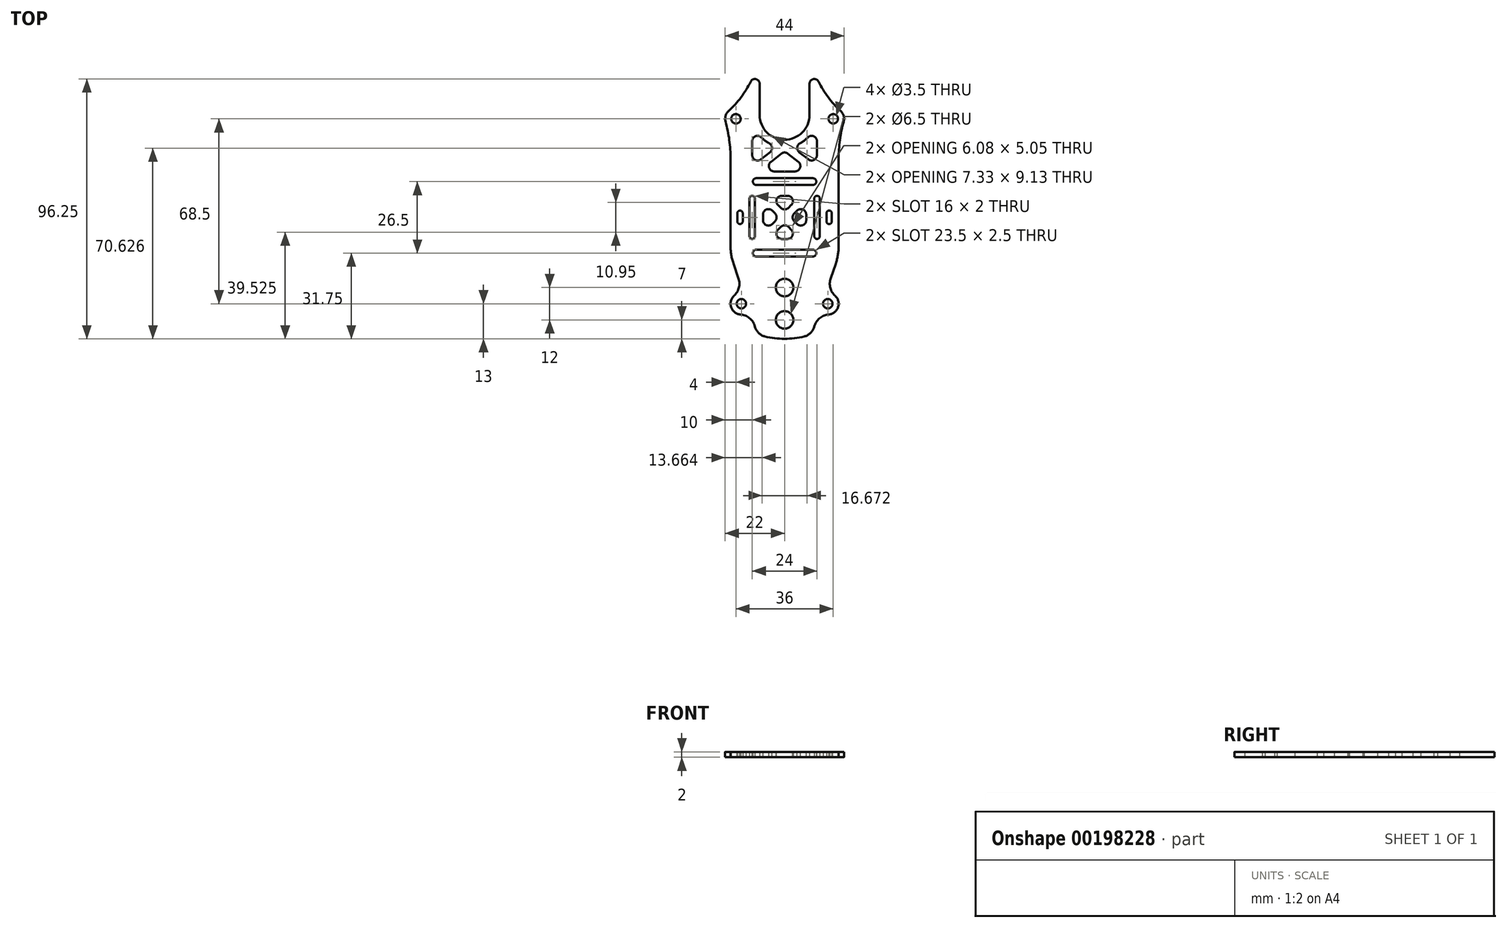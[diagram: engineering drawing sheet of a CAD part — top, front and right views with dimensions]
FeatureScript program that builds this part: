
annotation { "Feature Type Name" : "Feature", "Feature Type Description" : "" }
export const myFeature = defineFeature(function(context is Context, id is Id, definition is map)
    precondition{}
    {
        {
            var Q0;
            Q0=qCreatedBy(makeId("Top.planeOp"),FACE);
            var sketch = newSketch(context, id + "F0", { "sketchPlane" : qUnion([Q0])});
            skArc(sketch, "E0", {"start": v(-20.7, 39.46) * mm, "mid": v(-21.84, 37.62) * mm, "end": v(-21.86, 35.44) * mm});
            skLineSegment(sketch, "E1", {"start": v(-18.93, -17.14) * mm, "end": v(-17.05, -22.66) * mm});
            skLineSegment(sketch, "E2", {"start": v(0, 24) * mm, "end": v(0, -60) * mm, "construction": true});
            skCircle(sketch, "E3", {"center": v(-16, -32) * mm, "radius": 1.75 * mm});
            skArc(sketch, "E4.MirrorCS", {"start": v(20.7, 39.46) * mm, "mid": v(21.84, 37.62) * mm, "end": v(21.86, 35.44) * mm});
            skCircle(sketch, "E5.MirrorC", {"center": v(16, -32) * mm, "radius": 1.75 * mm});
            skLineSegment(sketch, "E6.MirrorCS", {"start": v(18.93, -17.14) * mm, "end": v(17.05, -22.66) * mm});
            skCircle(sketch, "E7", {"center": v(-18, 36.5) * mm, "radius": 1.75 * mm});
            skCircle(sketch, "E8.MirrorC", {"center": v(18, 36.5) * mm, "radius": 1.75 * mm});
            skCircle(sketch, "E9", {"center": v(0, -38) * mm, "radius": 3.25 * mm});
            skArc(sketch, "E10", {"start": v(-7.28, -44.13) * mm, "mid": v(-3.66, -44.78) * mm, "end": v(0, -45) * mm});
            skLineSegment(sketch, "E11.trimOffspring", {"start": v(-20, 21.67) * mm, "end": v(-20, -10.69) * mm});
            skArc(sketch, "E12", {"start": v(16.32, -35.99) * mm, "mid": v(19.79, -33.3) * mm, "end": v(18.7, -29.04) * mm});
            skArc(sketch, "E13.filletArc", {"start": v(16.32, -35.99) * mm, "mid": v(13.12, -37.23) * mm, "end": v(11.13, -40.03) * mm});
            skArc(sketch, "E14.filletArc", {"start": v(17.05, -22.66) * mm, "mid": v(16.92, -26.1) * mm, "end": v(18.7, -29.04) * mm});
            skArc(sketch, "E15.MirrorCS", {"start": v(-16.32, -35.99) * mm, "mid": v(-13.12, -37.23) * mm, "end": v(-11.13, -40.03) * mm});
            skArc(sketch, "E16.MirrorCS", {"start": v(-16.32, -35.99) * mm, "mid": v(-19.79, -33.3) * mm, "end": v(-18.7, -29.04) * mm});
            skArc(sketch, "E17.MirrorCS", {"start": v(-17.05, -22.66) * mm, "mid": v(-16.92, -26.1) * mm, "end": v(-18.7, -29.04) * mm});
            skLineSegment(sketch, "E18", {"start": v(-11.13, -40.03) * mm, "end": v(-10.84, -40.89) * mm});
            skLineSegment(sketch, "E19", {"start": v(11.13, -40.03) * mm, "end": v(10.84, -40.89) * mm});
            skLineSegment(sketch, "E20", {"start": v(-17.05, -22.66) * mm, "end": v(-11.13, -40.03) * mm, "construction": true});
            skLineSegment(sketch, "E21", {"start": v(17.05, -22.66) * mm, "end": v(11.13, -40.03) * mm, "construction": true});
            skArc(sketch, "E22", {"start": v(-9.25, 49.5) * mm, "mid": v(-10.6, 51.2) * mm, "end": v(-12.57, 50.27) * mm});
            skArc(sketch, "E23", {"start": v(-20.7, 39.46) * mm, "mid": v(-16.12, 44.48) * mm, "end": v(-12.57, 50.27) * mm});
            skArc(sketch, "E24.MirrorCS", {"start": v(9.25, 49.5) * mm, "mid": v(10.6, 51.2) * mm, "end": v(12.57, 50.27) * mm});
            skArc(sketch, "E25.MirrorCS", {"start": v(20.7, 39.46) * mm, "mid": v(16.12, 44.48) * mm, "end": v(12.57, 50.27) * mm});
            skPoint(sketch, "E26.visualSharp", {"position": v(-10, -43.34) * mm});
            skArc(sketch, "E26.filletArc", {"start": v(-10.84, -40.89) * mm, "mid": v(-9.47, -42.97) * mm, "end": v(-7.28, -44.13) * mm});
            skPoint(sketch, "E27.visualSharp", {"position": v(10, -43.34) * mm});
            skArc(sketch, "E27.filletArc", {"start": v(7.28, -44.13) * mm, "mid": v(9.47, -42.97) * mm, "end": v(10.84, -40.89) * mm});
            skLineSegment(sketch, "E28", {"start": v(-16.5, 1.5) * mm, "end": v(-16.5, -1.5) * mm, "construction": true});
            skArc(sketch, "E29.0.startCap", {"start": v(-17.5, 1.5) * mm, "mid": v(-16.5, 2.5) * mm, "end": v(-15.5, 1.5) * mm});
            skArc(sketch, "E29.0.endCap", {"start": v(-15.5, -1.5) * mm, "mid": v(-16.5, -2.5) * mm, "end": v(-17.5, -1.5) * mm});
            skLineSegment(sketch, "E29.0.left", {"start": v(-15.5, 1.5) * mm, "end": v(-15.5, -1.5) * mm});
            skLineSegment(sketch, "E29.0.right", {"start": v(-17.5, 1.5) * mm, "end": v(-17.5, -1.5) * mm});
            skLineSegment(sketch, "E30.MirrorCS", {"start": v(16.5, 1.5) * mm, "end": v(16.5, -1.5) * mm, "construction": true});
            skLineSegment(sketch, "E31.MirrorCS", {"start": v(15.5, 1.5) * mm, "end": v(15.5, -1.5) * mm});
            skLineSegment(sketch, "E32.MirrorCS", {"start": v(17.5, 1.5) * mm, "end": v(17.5, -1.5) * mm});
            skArc(sketch, "E33.MirrorCS", {"start": v(17.5, 1.5) * mm, "mid": v(16.5, 2.5) * mm, "end": v(15.5, 1.5) * mm});
            skArc(sketch, "E34.MirrorCS", {"start": v(15.5, -1.5) * mm, "mid": v(16.5, -2.5) * mm, "end": v(17.5, -1.5) * mm});
            skArc(sketch, "E35", {"start": v(-20, 21.67) * mm, "mid": v(-20.47, 28.62) * mm, "end": v(-21.86, 35.44) * mm});
            skArc(sketch, "E36.MirrorCS", {"start": v(20, 21.67) * mm, "mid": v(20.47, 28.62) * mm, "end": v(21.86, 35.44) * mm});
            skCircle(sketch, "E37", {"center": v(0, -38) * mm, "radius": 4.5 * mm, "construction": true});
            skLineSegment(sketch, "E38", {"start": v(20, 21.67) * mm, "end": v(20, -10.69) * mm});
            skLineSegment(sketch, "E39", {"start": v(-10.5, 13.25) * mm, "end": v(10.5, 13.25) * mm, "construction": true});
            skLineSegment(sketch, "E40", {"start": v(-10.5, -13.25) * mm, "end": v(10.5, -13.25) * mm, "construction": true});
            skArc(sketch, "E41.0.startCap", {"start": v(-10.5, 12) * mm, "mid": v(-11.75, 13.25) * mm, "end": v(-10.5, 14.5) * mm});
            skArc(sketch, "E41.0.endCap", {"start": v(10.5, 14.5) * mm, "mid": v(11.75, 13.25) * mm, "end": v(10.5, 12) * mm});
            skLineSegment(sketch, "E41.0.left", {"start": v(-10.5, 14.5) * mm, "end": v(10.5, 14.5) * mm});
            skLineSegment(sketch, "E41.0.right", {"start": v(-10.5, 12) * mm, "end": v(10.5, 12) * mm});
            skArc(sketch, "E41.1.startCap", {"start": v(-10.5, -14.5) * mm, "mid": v(-11.75, -13.25) * mm, "end": v(-10.5, -12) * mm});
            skArc(sketch, "E41.1.endCap", {"start": v(10.5, -12) * mm, "mid": v(11.75, -13.25) * mm, "end": v(10.5, -14.5) * mm});
            skLineSegment(sketch, "E41.1.left", {"start": v(-10.5, -12) * mm, "end": v(10.5, -12) * mm});
            skLineSegment(sketch, "E41.1.right", {"start": v(-10.5, -14.5) * mm, "end": v(10.5, -14.5) * mm});
            skPoint(sketch, "E42.visualSharp", {"position": v(-20, -14) * mm});
            skArc(sketch, "E42.filletArc", {"start": v(-20, -10.69) * mm, "mid": v(-19.73, -13.96) * mm, "end": v(-18.93, -17.14) * mm});
            skPoint(sketch, "E43.visualSharp", {"position": v(20, -14) * mm});
            skArc(sketch, "E43.filletArc", {"start": v(18.93, -17.14) * mm, "mid": v(19.73, -13.96) * mm, "end": v(20, -10.69) * mm});
            skLineSegment(sketch, "E44", {"start": v(-12, 7) * mm, "end": v(-12, -7) * mm, "construction": true});
            skLineSegment(sketch, "E45.MirrorCS", {"start": v(12, 7) * mm, "end": v(12, -7) * mm, "construction": true});
            skArc(sketch, "E46.0.startCap", {"start": v(-13, 7) * mm, "mid": v(-12, 8) * mm, "end": v(-11, 7) * mm});
            skArc(sketch, "E46.0.endCap", {"start": v(-11, -7) * mm, "mid": v(-12, -8) * mm, "end": v(-13, -7) * mm});
            skLineSegment(sketch, "E46.0.left", {"start": v(-11, 7) * mm, "end": v(-11, -7) * mm});
            skLineSegment(sketch, "E46.0.right", {"start": v(-13, 7) * mm, "end": v(-13, -7) * mm});
            skArc(sketch, "E46.3.startCap", {"start": v(11, 7) * mm, "mid": v(12, 8) * mm, "end": v(13, 7) * mm});
            skArc(sketch, "E46.3.endCap", {"start": v(13, -7) * mm, "mid": v(12, -8) * mm, "end": v(11, -7) * mm});
            skLineSegment(sketch, "E46.3.left", {"start": v(13, 7) * mm, "end": v(13, -7) * mm});
            skLineSegment(sketch, "E46.3.right", {"start": v(11, 7) * mm, "end": v(11, -7) * mm});
            skPoint(sketch, "E47.startSnap0", {"position": v(-16.5, 2.5) * mm});
            skArc(sketch, "E48.trimOffspring", {"start": v(0, -45) * mm, "mid": v(3.66, -44.78) * mm, "end": v(7.28, -44.13) * mm});
            skCircle(sketch, "E49", {"center": v(0, -26) * mm, "radius": 3.25 * mm});
            skLineSegment(sketch, "E50", {"start": v(-9.25, 49.5) * mm, "end": v(-9.25, 38) * mm});
            skLineSegment(sketch, "E51.MirrorCS", {"start": v(9.25, 49.5) * mm, "end": v(9.25, 38) * mm});
            skArc(sketch, "E52", {"start": v(-9.25, 38) * mm, "mid": v(0, 28.75) * mm, "end": v(9.25, 38) * mm});
            skSolve(sketch);
        }
        {
            var Q0;
            Q0=qSketchRegion(id+"F0",true);
            var Q1;
            Q1=makeQuery(id+"F0.imprint","IMPRINT",FACE,{"disambiguationData":[TD([[makeQuery(id+"F0.imprint","IMPRINT",EDGE,{"derivedFrom":sQuery(id+"F0.wireOp",EDGE,"f439a884-37bc-483a-9020-57d0572b4fa8.sketch_text.stroke-0")}),-1.0]])]});
            var Q2;
            Q2=makeQuery(id+"F0.imprint","IMPRINT",FACE,{"disambiguationData":[TD([[makeQuery(id+"F0.imprint","IMPRINT",EDGE,{"derivedFrom":sQuery(id+"F0.wireOp",EDGE,"f439a884-37bc-483a-9020-57d0572b4fa8.sketch_text.stroke-27")}),-1.0]])]});
            extrude(context, id + "F1", {"entities" : qUnion([Q0, Q1, Q2]), "depth" : 2 * mm});
        }
        {
            var Q0;
            Q0=makeQuery(id+"F1.opExtrude","CAP_FACE",FACE,{"disambiguationData":[OSD([sQuery(id+"F0.wireOp",EDGE,"E0"),sQuery(id+"F0.wireOp",EDGE,"E1"),sQuery(id+"F0.wireOp",EDGE,"E3"),sQuery(id+"F0.wireOp",EDGE,"E4.MirrorCS"),sQuery(id+"F0.wireOp",EDGE,"E5.MirrorC"),sQuery(id+"F0.wireOp",EDGE,"E6.MirrorCS"),sQuery(id+"F0.wireOp",EDGE,"E7"),sQuery(id+"F0.wireOp",EDGE,"E8.MirrorC"),sQuery(id+"F0.wireOp",EDGE,"E9"),sQuery(id+"F0.wireOp",EDGE,"E10"),sQuery(id+"F0.wireOp",EDGE,"E11.trimOffspring"),sQuery(id+"F0.wireOp",EDGE,"E12"),sQuery(id+"F0.wireOp",EDGE,"E13.filletArc"),sQuery(id+"F0.wireOp",EDGE,"E14.filletArc"),sQuery(id+"F0.wireOp",EDGE,"E15.MirrorCS"),sQuery(id+"F0.wireOp",EDGE,"E16.MirrorCS"),sQuery(id+"F0.wireOp",EDGE,"E17.MirrorCS"),sQuery(id+"F0.wireOp",EDGE,"E18"),sQuery(id+"F0.wireOp",EDGE,"E19"),sQuery(id+"F0.wireOp",EDGE,"E22"),sQuery(id+"F0.wireOp",EDGE,"E23"),sQuery(id+"F0.wireOp",EDGE,"E24.MirrorCS"),sQuery(id+"F0.wireOp",EDGE,"E25.MirrorCS"),sQuery(id+"F0.wireOp",EDGE,"E26.filletArc"),sQuery(id+"F0.wireOp",EDGE,"E27.filletArc"),sQuery(id+"F0.wireOp",EDGE,"E29.0.startCap"),sQuery(id+"F0.wireOp",EDGE,"E29.0.endCap"),sQuery(id+"F0.wireOp",EDGE,"E29.0.left"),sQuery(id+"F0.wireOp",EDGE,"E29.0.right"),sQuery(id+"F0.wireOp",EDGE,"E31.MirrorCS"),sQuery(id+"F0.wireOp",EDGE,"E32.MirrorCS"),sQuery(id+"F0.wireOp",EDGE,"E33.MirrorCS"),sQuery(id+"F0.wireOp",EDGE,"E34.MirrorCS"),sQuery(id+"F0.wireOp",EDGE,"E35"),sQuery(id+"F0.wireOp",EDGE,"E36.MirrorCS"),sQuery(id+"F0.wireOp",EDGE,"E38"),sQuery(id+"F0.wireOp",EDGE,"E41.0.startCap"),sQuery(id+"F0.wireOp",EDGE,"E41.0.endCap"),sQuery(id+"F0.wireOp",EDGE,"E41.0.left"),sQuery(id+"F0.wireOp",EDGE,"E41.0.right"),sQuery(id+"F0.wireOp",EDGE,"E41.1.startCap"),sQuery(id+"F0.wireOp",EDGE,"E41.1.endCap"),sQuery(id+"F0.wireOp",EDGE,"E41.1.left"),sQuery(id+"F0.wireOp",EDGE,"E41.1.right"),sQuery(id+"F0.wireOp",EDGE,"E42.filletArc"),sQuery(id+"F0.wireOp",EDGE,"E43.filletArc"),sQuery(id+"F0.wireOp",EDGE,"E46.0.startCap"),sQuery(id+"F0.wireOp",EDGE,"E46.0.endCap"),sQuery(id+"F0.wireOp",EDGE,"E46.0.left"),sQuery(id+"F0.wireOp",EDGE,"E46.0.right"),sQuery(id+"F0.wireOp",EDGE,"E46.3.startCap"),sQuery(id+"F0.wireOp",EDGE,"E46.3.endCap"),sQuery(id+"F0.wireOp",EDGE,"E46.3.left"),sQuery(id+"F0.wireOp",EDGE,"E46.3.right"),sQuery(id+"F0.wireOp",EDGE,"E48.trimOffspring"),sQuery(id+"F0.wireOp",EDGE,"E49"),sQuery(id+"F0.wireOp",EDGE,"E50"),sQuery(id+"F0.wireOp",EDGE,"E51.MirrorCS"),sQuery(id+"F0.wireOp",EDGE,"E52")])],"isStart":false});
            var sketch = newSketch(context, id + "F2", { "sketchPlane" : qUnion([Q0])});
            skLineSegment(sketch, "E53.bottom", {"start": v(-1.05, 8) * mm, "end": v(1.05, 8) * mm});
            skLineSegment(sketch, "E53.top", {"start": v(-1.05, -8) * mm, "end": v(1.05, -8) * mm});
            skLineSegment(sketch, "E53.left", {"start": v(-8, 1.05) * mm, "end": v(-8, -1.05) * mm});
            skLineSegment(sketch, "E53.right", {"start": v(8, 1.05) * mm, "end": v(8, -1.05) * mm});
            skLineSegment(sketch, "E54.bottom", {"start": v(-12, 36) * mm, "end": v(12, 36) * mm, "construction": true});
            skLineSegment(sketch, "E54.top", {"start": v(-3.83, 17) * mm, "end": v(3.83, 17) * mm});
            skLineSegment(sketch, "E54.left", {"start": v(-12, 28.2) * mm, "end": v(-12, 23.05) * mm});
            skLineSegment(sketch, "E54.right", {"start": v(12, 28.2) * mm, "end": v(12, 23.05) * mm});
            skArc(sketch, "E55", {"start": v(-8.57, 29.6) * mm, "mid": v(-7.22, 28.42) * mm, "end": v(-5.71, 27.45) * mm});
            skPoint(sketch, "E55.centerSnap0", {"position": v(0, 36) * mm});
            skLineSegment(sketch, "E56", {"start": v(-8, 8) * mm, "end": v(8, -8) * mm, "construction": true});
            skLineSegment(sketch, "E57", {"start": v(-8, -8) * mm, "end": v(8, 8) * mm, "construction": true});
            skLineSegment(sketch, "E58", {"start": v(-12, 36) * mm, "end": v(12, 17) * mm, "construction": true});
            skLineSegment(sketch, "E59", {"start": v(-12, 17) * mm, "end": v(12, 36) * mm, "construction": true});
            skLineSegment(sketch, "E60", {"start": v(1.24, 23.6) * mm, "end": v(5.08, 20.57) * mm});
            skLineSegment(sketch, "E61", {"start": v(5.42, 24.12) * mm, "end": v(8.76, 21.48) * mm});
            skLineSegment(sketch, "E62.MirrorCS", {"start": v(-5.42, 24.12) * mm, "end": v(-8.76, 21.48) * mm});
            skLineSegment(sketch, "E63.MirrorCS", {"start": v(-1.24, 23.6) * mm, "end": v(-5.08, 20.57) * mm});
            skArc(sketch, "E64.trimOffspring", {"start": v(5.71, 27.45) * mm, "mid": v(7.22, 28.42) * mm, "end": v(8.57, 29.6) * mm});
            skPoint(sketch, "E65.orphan", {"position": v(2, 26.17) * mm});
            skPoint(sketch, "E66.orphan", {"position": v(-2, 26.17) * mm});
            skLineSegment(sketch, "E67", {"start": v(-12, 38) * mm, "end": v(-12, 36) * mm, "construction": true});
            skLineSegment(sketch, "E68", {"start": v(12, 38) * mm, "end": v(12, 36) * mm, "construction": true});
            skPoint(sketch, "E69.visualSharp", {"position": v(-12, 38) * mm});
            skArc(sketch, "E69.filletArc", {"start": v(-8.57, 29.6) * mm, "mid": v(-10.76, 30.05) * mm, "end": v(-12, 28.2) * mm});
            skPoint(sketch, "E70.visualSharp", {"position": v(-2.67, 26.3) * mm});
            skArc(sketch, "E70.filletArc", {"start": v(-5.42, 24.12) * mm, "mid": v(-4.67, 25.86) * mm, "end": v(-5.71, 27.45) * mm});
            skPoint(sketch, "E71.visualSharp", {"position": v(-12, 18.91) * mm});
            skArc(sketch, "E71.filletArc", {"start": v(-12, 23.05) * mm, "mid": v(-10.87, 21.25) * mm, "end": v(-8.76, 21.48) * mm});
            skPoint(sketch, "E72.visualSharp", {"position": v(-9.58, 17) * mm});
            skArc(sketch, "E72.filletArc", {"start": v(-5.08, 20.57) * mm, "mid": v(-5.72, 18.34) * mm, "end": v(-3.83, 17) * mm});
            skPoint(sketch, "E73.visualSharp", {"position": v(9.58, 17) * mm});
            skArc(sketch, "E73.filletArc", {"start": v(3.83, 17) * mm, "mid": v(5.72, 18.34) * mm, "end": v(5.08, 20.57) * mm});
            skPoint(sketch, "E74.visualSharp", {"position": v(0, 24.59) * mm});
            skArc(sketch, "E74.filletArc", {"start": v(1.24, 23.6) * mm, "mid": v(0, 24.04) * mm, "end": v(-1.24, 23.6) * mm});
            skPoint(sketch, "E75.visualSharp", {"position": v(2.67, 26.3) * mm});
            skArc(sketch, "E75.filletArc", {"start": v(5.71, 27.45) * mm, "mid": v(4.67, 25.86) * mm, "end": v(5.42, 24.12) * mm});
            skPoint(sketch, "E76.visualSharp", {"position": v(12, 18.91) * mm});
            skArc(sketch, "E76.filletArc", {"start": v(8.76, 21.48) * mm, "mid": v(10.87, 21.25) * mm, "end": v(12, 23.05) * mm});
            skPoint(sketch, "E77.visualSharp", {"position": v(12, 38) * mm});
            skArc(sketch, "E77.filletArc", {"start": v(12, 28.2) * mm, "mid": v(10.76, 30.05) * mm, "end": v(8.57, 29.6) * mm});
            skLineSegment(sketch, "E78", {"start": v(-2.46, 4.59) * mm, "end": v(-1.41, 3.54) * mm});
            skLineSegment(sketch, "E79", {"start": v(-4.59, 2.46) * mm, "end": v(-3.54, 1.41) * mm});
            skLineSegment(sketch, "E80.MirrorCS", {"start": v(2.46, 4.59) * mm, "end": v(1.41, 3.54) * mm});
            skLineSegment(sketch, "E81.MirrorCS", {"start": v(4.59, 2.46) * mm, "end": v(3.54, 1.41) * mm});
            skLineSegment(sketch, "E82.trimOffspring", {"start": v(-3.54, -1.41) * mm, "end": v(-4.59, -2.46) * mm});
            skLineSegment(sketch, "E83.trimOffspring", {"start": v(1.41, -3.54) * mm, "end": v(2.46, -4.59) * mm});
            skLineSegment(sketch, "E84.trimOffspring", {"start": v(-1.41, -3.54) * mm, "end": v(-2.46, -4.59) * mm});
            skLineSegment(sketch, "E85.trimOffspring", {"start": v(3.54, -1.41) * mm, "end": v(4.59, -2.46) * mm});
            skPoint(sketch, "E86.visualSharp", {"position": v(-5.88, 8) * mm});
            skArc(sketch, "E86.filletArc", {"start": v(-1.05, 8) * mm, "mid": v(-2.9, 6.77) * mm, "end": v(-2.46, 4.59) * mm});
            skPoint(sketch, "E87.visualSharp", {"position": v(5.88, 8) * mm});
            skArc(sketch, "E87.filletArc", {"start": v(2.46, 4.59) * mm, "mid": v(2.9, 6.77) * mm, "end": v(1.05, 8) * mm});
            skPoint(sketch, "E88.visualSharp", {"position": v(0, 2.12) * mm});
            skArc(sketch, "E88.filletArc", {"start": v(-1.41, 3.54) * mm, "mid": v(0, 2.95) * mm, "end": v(1.41, 3.54) * mm});
            skPoint(sketch, "E89.visualSharp", {"position": v(-8, 5.88) * mm});
            skArc(sketch, "E89.filletArc", {"start": v(-4.59, 2.46) * mm, "mid": v(-6.77, 2.9) * mm, "end": v(-8, 1.05) * mm});
            skPoint(sketch, "E90.visualSharp", {"position": v(-8, -5.88) * mm});
            skArc(sketch, "E90.filletArc", {"start": v(-8, -1.05) * mm, "mid": v(-6.77, -2.9) * mm, "end": v(-4.59, -2.46) * mm});
            skPoint(sketch, "E91.visualSharp", {"position": v(-5.88, -8) * mm});
            skArc(sketch, "E91.filletArc", {"start": v(-2.46, -4.59) * mm, "mid": v(-2.9, -6.77) * mm, "end": v(-1.05, -8) * mm});
            skPoint(sketch, "E92.visualSharp", {"position": v(-2.12, 0) * mm});
            skArc(sketch, "E92.filletArc", {"start": v(-3.54, -1.41) * mm, "mid": v(-2.95, 0) * mm, "end": v(-3.54, 1.41) * mm});
            skPoint(sketch, "E93.visualSharp", {"position": v(5.88, -8) * mm});
            skArc(sketch, "E93.filletArc", {"start": v(1.05, -8) * mm, "mid": v(2.9, -6.77) * mm, "end": v(2.46, -4.59) * mm});
            skPoint(sketch, "E94.visualSharp", {"position": v(0, -2.12) * mm});
            skArc(sketch, "E94.filletArc", {"start": v(1.41, -3.54) * mm, "mid": v(0, -2.95) * mm, "end": v(-1.41, -3.54) * mm});
            skPoint(sketch, "E95.visualSharp", {"position": v(2.12, 0) * mm});
            skArc(sketch, "E95.filletArc", {"start": v(3.54, 1.41) * mm, "mid": v(2.95, 0) * mm, "end": v(3.54, -1.41) * mm});
            skPoint(sketch, "E96.visualSharp", {"position": v(8, -5.88) * mm});
            skArc(sketch, "E96.filletArc", {"start": v(4.59, -2.46) * mm, "mid": v(6.77, -2.9) * mm, "end": v(8, -1.05) * mm});
            skPoint(sketch, "E97.visualSharp", {"position": v(8, 5.88) * mm});
            skArc(sketch, "E97.filletArc", {"start": v(8, 1.05) * mm, "mid": v(6.77, 2.9) * mm, "end": v(4.59, 2.46) * mm});
            skSolve(sketch);
        }
        {
            var Q0;
            Q0 = qSketchRegion(id + "F2", true);
            extrude(context, id + "F3", {"entities" : qUnion([Q0]), "operationType" : NewBodyOperationType.REMOVE, "oppositeDirection" : true, "depth" : 25 * mm});
        }
    });
